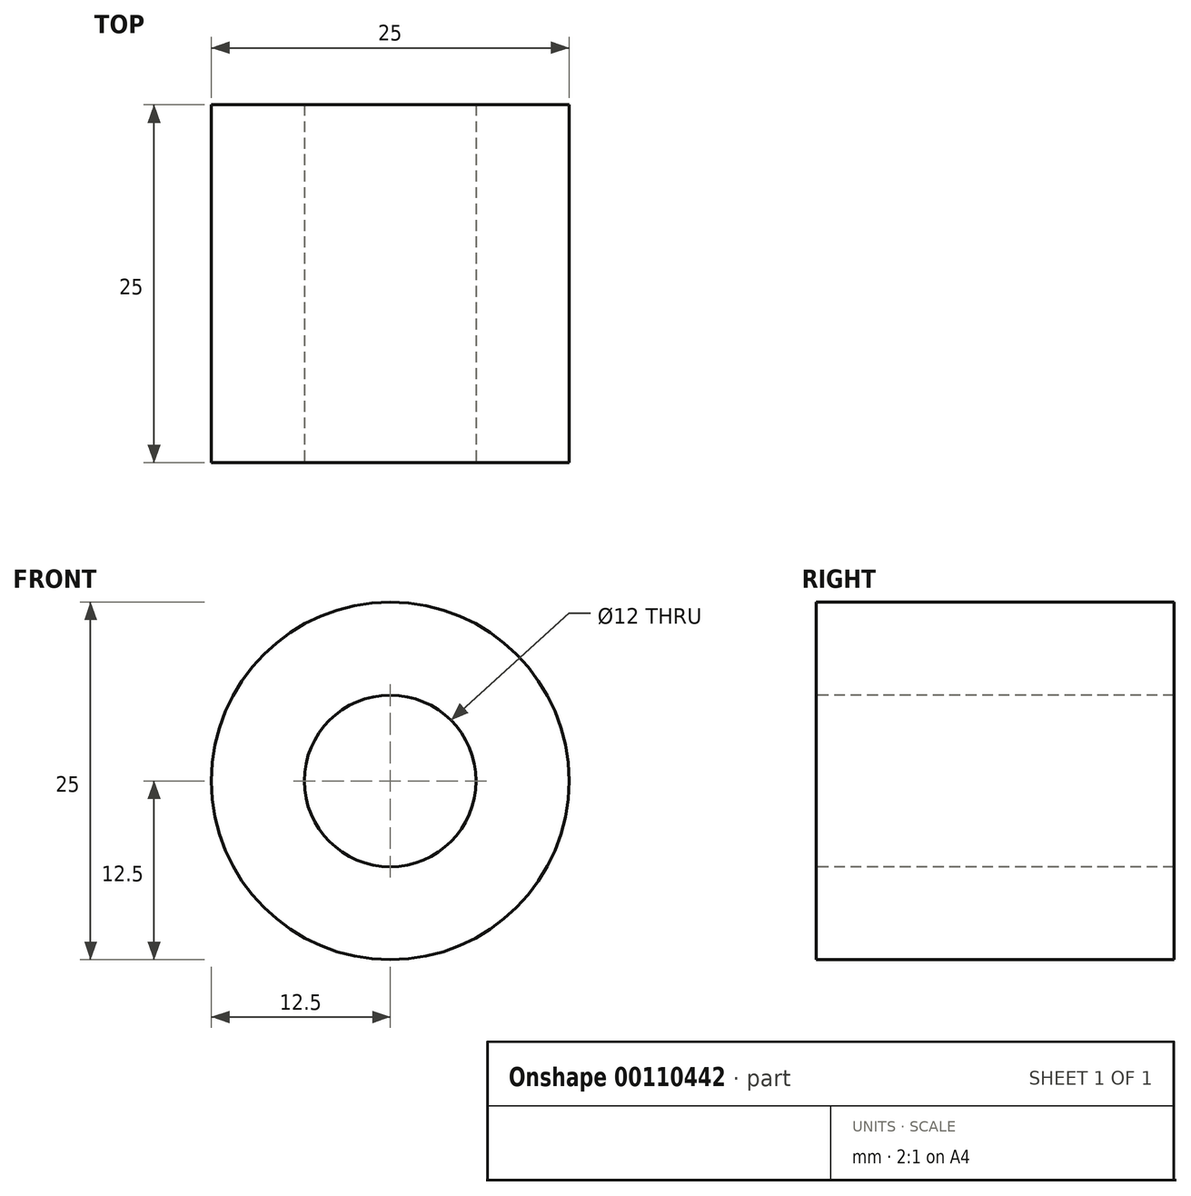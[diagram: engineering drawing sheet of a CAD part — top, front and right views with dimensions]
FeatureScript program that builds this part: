
annotation { "Feature Type Name" : "Feature", "Feature Type Description" : "" }
export const myFeature = defineFeature(function(context is Context, id is Id, definition is map)
    precondition{}
    {
        {
            var Q0;
            Q0=qCreatedBy(makeId("Top.planeOp"),FACE);
            var sketch = newSketch(context, id + "F0", { "sketchPlane" : qUnion([Q0])});
            skLineSegment(sketch, "E0.bottom", {"start": v(12.5, 0) * mm, "end": v(-12.5, 0) * mm});
            skLineSegment(sketch, "E0.top", {"start": v(12.5, 25) * mm, "end": v(-12.5, 25) * mm});
            skLineSegment(sketch, "E0.left", {"start": v(12.5, 0) * mm, "end": v(12.5, 25) * mm});
            skLineSegment(sketch, "E0.right", {"start": v(-12.5, 0) * mm, "end": v(-12.5, 25) * mm});
            skLineSegment(sketch, "E1.bottom", {"start": v(137.5, 12.8) * mm, "end": v(162.5, 12.8) * mm});
            skLineSegment(sketch, "E1.top", {"start": v(137.5, -12.2) * mm, "end": v(162.5, -12.2) * mm});
            skLineSegment(sketch, "E1.left", {"start": v(137.5, 12.8) * mm, "end": v(137.5, -12.2) * mm});
            skLineSegment(sketch, "E1.right", {"start": v(162.5, 12.8) * mm, "end": v(162.5, -12.2) * mm});
            skPoint(sketch, "E2.endSnap0", {"position": v(162.5, 0.3) * mm});
            skLineSegment(sketch, "E3", {"start": v(0, 32.15) * mm, "end": v(0, -10.9) * mm, "construction": true});
            skPoint(sketch, "E3.endSnap0", {"position": v(0, 25) * mm});
            skLineSegment(sketch, "E4", {"start": v(-6.25, 25) * mm, "end": v(-6.25, 0) * mm, "construction": true});
            skLineSegment(sketch, "E5", {"start": v(6.25, 0) * mm, "end": v(6.25, 25) * mm, "construction": true});
            skLineSegment(sketch, "E6", {"start": v(150, 18.62) * mm, "end": v(150, -18.29) * mm, "construction": true});
            skPoint(sketch, "E6.startSnap0", {"position": v(150, 12.8) * mm});
            skLineSegment(sketch, "E7", {"start": v(143.75, -12.2) * mm, "end": v(143.75, 12.8) * mm, "construction": true});
            skLineSegment(sketch, "E8", {"start": v(156.25, 12.8) * mm, "end": v(156.25, -12.2) * mm, "construction": true});
            skLineSegment(sketch, "E9", {"start": v(11.88, 12) * mm, "end": v(25, 12) * mm});
            skPoint(sketch, "E9.endSnap0", {"position": v(11.88, 12) * mm});
            skFitSpline(sketch, "E10", {"points": [v(25, 12) * mm, v(96.88, 0) * mm, v(137.5, -0.2) * mm], "startDerivative": vector(25.37, 0) * mm, "endDerivative": vector(87.73, -1.46) * mm, "construction": true});
            skSolve(sketch);
        }
        {
            var Q0;
            Q0=qCreatedBy(makeId("Front.planeOp"),FACE);
            var sketch = newSketch(context, id + "F1", { "sketchPlane" : qUnion([Q0])});
            skCircle(sketch, "E11", {"center": v(0, 0) * mm, "radius": 6 * mm});
            skCircle(sketch, "E12", {"center": v(0, 0) * mm, "radius": 12.5 * mm});
            skSolve(sketch);
        }
        {
            var Q0;
            Q0=makeQuery(id+"F1.imprint","IMPRINT",FACE,{"disambiguationData":[TD([[makeQuery(id+"F1.imprint","IMPRINT",EDGE,{"derivedFrom":sQuery(id+"F1.wireOp",EDGE,"E11")}),-1.0]])]});
            var Q1;
            Q1=makeQuery(id+"F1.imprint","IMPRINT",FACE,{"disambiguationData":[TD([[makeQuery(id+"F1.imprint","IMPRINT",EDGE,{"derivedFrom":sQuery(id+"F1.wireOp",EDGE,"d58d475f-7a0f-42f6-86ab-05f3cd3ce635.1.0.0")}),-1.0]])]});
            extrude(context, id + "F2", {"entities" : qUnion([Q0, Q1]), "oppositeDirection" : true, "depth" : 25 * mm});
        }
    });
